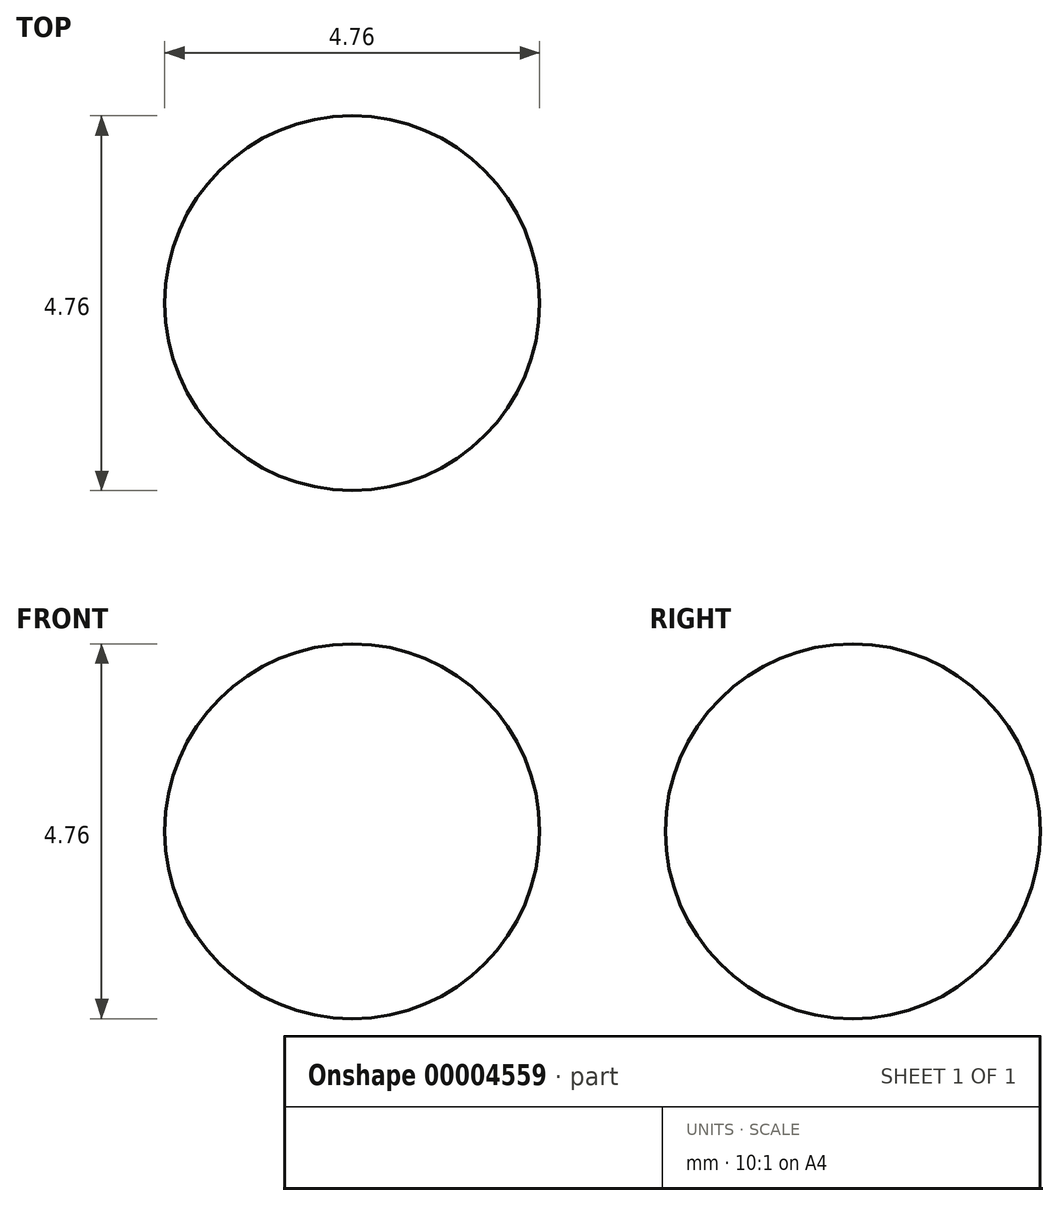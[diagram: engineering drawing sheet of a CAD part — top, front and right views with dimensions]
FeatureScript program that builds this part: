
annotation { "Feature Type Name" : "Feature", "Feature Type Description" : "" }
export const myFeature = defineFeature(function(context is Context, id is Id, definition is map)
    precondition{}
    {
        {
            var Q0;
            Q0=qCreatedBy(makeId("Top.planeOp"),FACE);
            var sketch = newSketch(context, id + "F0", { "sketchPlane" : qUnion([Q0])});
            skArc(sketch, "E0", {"start": v(0, -2.38) * mm, "mid": v(2.38, 0) * mm, "end": v(0, 2.38) * mm});
            skLineSegment(sketch, "E1", {"start": v(0, -2.38) * mm, "end": v(0, 2.38) * mm});
            skSolve(sketch);
        }
        {
            var Q0;
            Q0=makeQuery(id+"F0.imprint","IMPRINT",FACE,{"disambiguationData":[TD([[makeQuery(id+"F0.imprint","IMPRINT",EDGE,{"derivedFrom":sQuery(id+"F0.wireOp",EDGE,"E0")}),1.0]])]});
            var Q1;
            Q1=sQuery(id+"F0.wireOp",EDGE,"E1");
            revolve(context, id + "F1", {"entities" : qUnion([Q0]), "axis" : qUnion([Q1]), "revolveType" : RevolveType.FULL});
        }
    });
